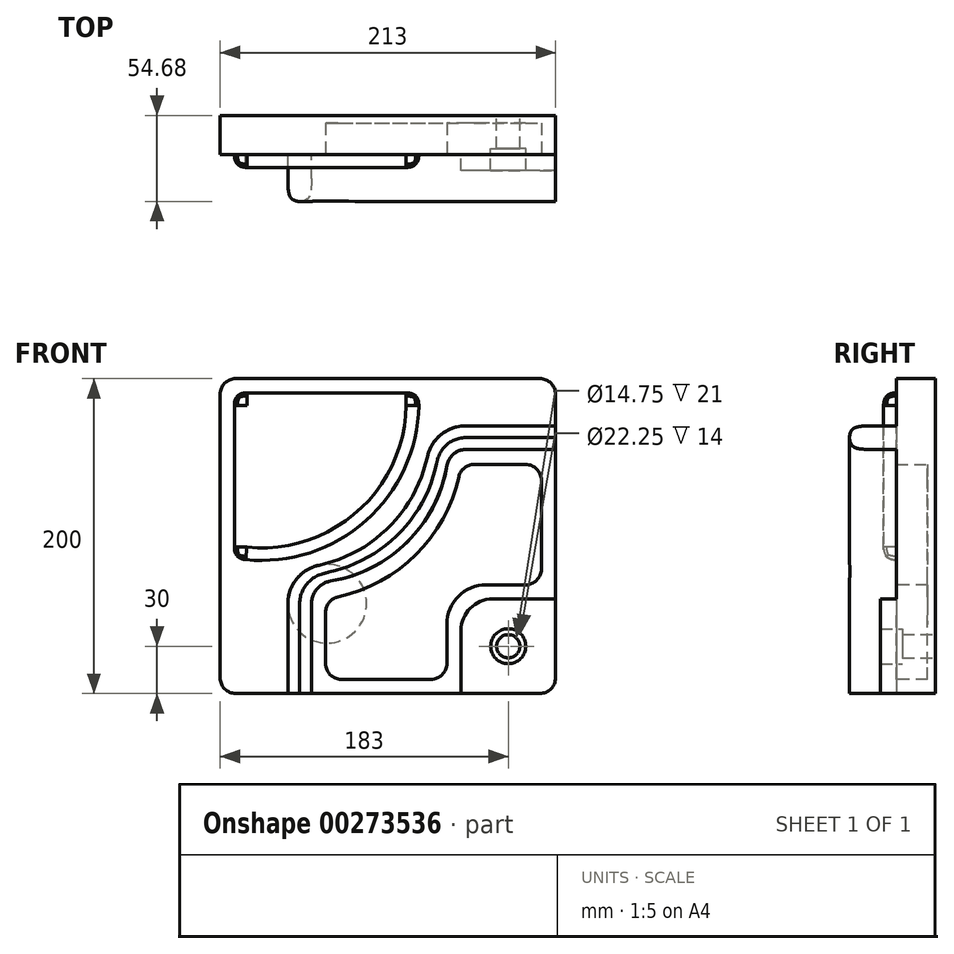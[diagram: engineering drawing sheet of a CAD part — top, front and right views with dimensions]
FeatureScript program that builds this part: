
annotation { "Feature Type Name" : "Feature", "Feature Type Description" : "" }
export const myFeature = defineFeature(function(context is Context, id is Id, definition is map)
    precondition{}
    {
        {
            var Q0;
            Q0=qCreatedBy(makeId("Front.planeOp"),FACE);
            var sketch = newSketch(context, id + "F0", { "sketchPlane" : qUnion([Q0])});
            skLineSegment(sketch, "E0", {"start": v(213, 0) * mm, "end": v(213, -200) * mm});
            skLineSegment(sketch, "E1", {"start": v(213, -200) * mm, "end": v(0, -200) * mm});
            skLineSegment(sketch, "E2", {"start": v(213, 0) * mm, "end": v(0, 0) * mm});
            skLineSegment(sketch, "E3", {"start": v(0, 0) * mm, "end": v(0, -200) * mm});
            skSolve(sketch);
        }
        {
            var Q0;
            Q0 = qSketchRegion(id + "F0", true);
            extrude(context, id + "F1", {"entities" : qUnion([Q0]), "oppositeDirection" : true, "depth" : 25 * mm});
        }
        {
            var Q0;
            Q0=makeQuery(id+"F1.opExtrude","CAP_FACE",FACE,{"disambiguationData":[OSD([sQuery(id+"F0.wireOp",EDGE,"E0"),sQuery(id+"F0.wireOp",EDGE,"E1"),sQuery(id+"F0.wireOp",EDGE,"E2"),sQuery(id+"F0.wireOp",EDGE,"E3")])],"isStart":true});
            var sketch = newSketch(context, id + "F2", { "sketchPlane" : qUnion([Q0])});
            skLineSegment(sketch, "E4", {"start": v(213, -200) * mm, "end": v(213, -140) * mm});
            skLineSegment(sketch, "E5", {"start": v(213, -140) * mm, "end": v(153, -140) * mm});
            skLineSegment(sketch, "E6", {"start": v(153, -140) * mm, "end": v(153, -200) * mm});
            skLineSegment(sketch, "E7", {"start": v(153, -200) * mm, "end": v(213, -200) * mm});
            skSolve(sketch);
        }
        {
            var Q0;
            Q0 = qSketchRegion(id + "F2", true);
            extrude(context, id + "F3", {"entities" : qUnion([Q0]), "operationType" : NewBodyOperationType.ADD, "depth" : 10 * mm});
        }
        {
            var Q0;
            Q0=makeQuery(id+"F3.boolean.opBoolean","MERGE",EDGE,{"derivedFrom":[makeQuery(id+"F1.opExtrude","SWEPT_EDGE",EDGE,{"disambiguationData":[OSD([sQuery(id+"F0.wireOp",EDGE,"E0"),sQuery(id+"F0.wireOp",EDGE,"E1")])]}),makeQuery(id+"F3.opExtrude","SWEPT_EDGE",EDGE,{"disambiguationData":[OSD([sQuery(id+"F2.wireOp",EDGE,"E4"),sQuery(id+"F2.wireOp",EDGE,"E7")])]})]});
            var Q1;
            Q1=makeQuery(id+"F1.opExtrude","SWEPT_EDGE",EDGE,{"disambiguationData":[OSD([sQuery(id+"F0.wireOp",EDGE,"E0"),sQuery(id+"F0.wireOp",EDGE,"E2")])]});
            var Q2;
            Q2=makeQuery(id+"F1.opExtrude","SWEPT_EDGE",EDGE,{"disambiguationData":[OSD([sQuery(id+"F0.wireOp",EDGE,"E2"),sQuery(id+"F0.wireOp",EDGE,"E3")])]});
            var Q3;
            Q3=makeQuery(id+"F1.opExtrude","SWEPT_EDGE",EDGE,{"disambiguationData":[OSD([sQuery(id+"F0.wireOp",EDGE,"E1"),sQuery(id+"F0.wireOp",EDGE,"E3")])]});
            fillet(context, id + "F4", {"entities" : qUnion([Q0, Q1, Q2, Q3]), "radius" : 10 * mm, "tangentPropagation" : true, "allowEdgeOverflow" : false});
        }
        {
            var Q0;
            Q0=makeQuery(id+"F1.opExtrude","CAP_FACE",FACE,{"disambiguationData":[OSD([sQuery(id+"F0.wireOp",EDGE,"E0"),sQuery(id+"F0.wireOp",EDGE,"E1"),sQuery(id+"F0.wireOp",EDGE,"E2"),sQuery(id+"F0.wireOp",EDGE,"E3")])],"isStart":true});
            var sketch = newSketch(context, id + "F5", { "sketchPlane" : qUnion([Q0])});
            skLineSegment(sketch, "E8", {"start": v(43, -143) * mm, "end": v(43, -200) * mm});
            skLineSegment(sketch, "E9", {"start": v(213, -30) * mm, "end": v(156, -30) * mm});
            skLineSegment(sketch, "E10", {"start": v(213, -30) * mm, "end": v(213, -45) * mm});
            skLineSegment(sketch, "E11", {"start": v(43, -200) * mm, "end": v(58, -200) * mm});
            skLineSegment(sketch, "E12", {"start": v(213, -45) * mm, "end": v(156, -45) * mm});
            skLineSegment(sketch, "E13", {"start": v(58, -200) * mm, "end": v(58, -143) * mm});
            skArc(sketch, "E14", {"start": v(70.2, -128.6) * mm, "mid": v(118.95, -103.6) * mm, "end": v(144.17, -54.98) * mm});
            skArc(sketch, "E15", {"start": v(62.7, -118.57) * mm, "mid": v(107.25, -94.25) * mm, "end": v(131.57, -49.7) * mm});
            skArc(sketch, "E16", {"start": v(156, -30) * mm, "mid": v(140.3, -35.54) * mm, "end": v(131.57, -49.7) * mm});
            skArc(sketch, "E17", {"start": v(62.7, -118.57) * mm, "mid": v(48.54, -127.3) * mm, "end": v(43, -143) * mm});
            skArc(sketch, "E18", {"start": v(70.2, -128.6) * mm, "mid": v(61.46, -133.57) * mm, "end": v(58, -143) * mm});
            skArc(sketch, "E19", {"start": v(156, -45) * mm, "mid": v(148.26, -47.83) * mm, "end": v(144.17, -54.98) * mm});
            skSolve(sketch);
        }
        {
            var Q0;
            Q0 = qSketchRegion(id + "F5", true);
            extrude(context, id + "F6", {"entities" : qUnion([Q0]), "operationType" : NewBodyOperationType.ADD, "depth" : 30 * mm});
        }
        {
            var Q0;
            Q0=makeQuery(id+"F6.opExtrude","CAP_EDGE",EDGE,{"disambiguationData":[OSD([sQuery(id+"F5.wireOp",EDGE,"E13")])],"isStart":false});
            var Q1;
            Q1=makeQuery(id+"F6.opExtrude","CAP_EDGE",EDGE,{"disambiguationData":[OSD([sQuery(id+"F5.wireOp",EDGE,"E8")])],"isStart":false});
            fillet(context, id + "F7", {"entities" : qUnion([Q0, Q1]), "radius" : 15 * mm, "tangentPropagation" : true, "rho" : 0.7, "crossSection" : FilletCrossSection.CONIC, "allowEdgeOverflow" : false});
        }
        {
            var Q0;
            Q0=makeQuery(id+"F3.opExtrude","CAP_FACE",FACE,{"disambiguationData":[OSD([sQuery(id+"F2.wireOp",EDGE,"E4"),sQuery(id+"F2.wireOp",EDGE,"E5"),sQuery(id+"F2.wireOp",EDGE,"E6"),sQuery(id+"F2.wireOp",EDGE,"E7")])],"isStart":false});
            var sketch = newSketch(context, id + "F8", { "sketchPlane" : qUnion([Q0])});
            skPoint(sketch, "E20", {"position": v(183, -170) * mm});
            skSolve(sketch);
        }
        {
            var Q0;
            Q0=sQuery(id+"F8.wireOp",VERTEX,"E20");
            var Q1;
            Q1=makeQuery(id+"F1.opExtrude","SWEPT_BODY",BODY,{"disambiguationData":[OSD([sQuery(id+"F0.wireOp",EDGE,"E0"),sQuery(id+"F0.wireOp",EDGE,"E1"),sQuery(id+"F0.wireOp",EDGE,"E2"),sQuery(id+"F0.wireOp",EDGE,"E3")])]});
            hole(context, id + "F9", {"style" : HoleStyle.C_BORE, "endStyle" : HoleEndStyle.THROUGH, "standardTappedOrClearance" : lookupTablePath({ "standard" : "ISO", "fit" : "Close", "size" : "M14", "type" : "Clearance" }), "standardBlindInLast" : lookupTablePath({ "fit" : "Close", "standard" : "ISO", "size" : "M14", "type" : "Clearance" }), "holeDiameter" : 14.75 * mm, "cBoreDiameter" : 22.25 * mm, "cBoreDepth" : 14 * mm, "tappedDepth" : 12 * mm, "tapClearance" : 3, "locations" : qUnion([Q0]), "scope" : qUnion([Q1])});
        }
        {
            var Q0;
            {var subQ0=sQuery(id+"F0.wireOp",EDGE,"E3");var subQ1=sQuery(id+"F0.wireOp",EDGE,"E2");var subQ2=sQuery(id+"F0.wireOp",EDGE,"E1");var subQ3=sQuery(id+"F0.wireOp",EDGE,"E0");Q0=makeQuery(id+"F6.boolean.opBoolean","SPLIT",FACE,{"disambiguationData":[TD([makeQuery(id+"F1.opExtrude","SWEPT_FACE",FACE,{"disambiguationData":[OSD([subQ1])]})])],"derivedFrom":makeQuery(id+"F1.opExtrude","CAP_FACE",FACE,{"disambiguationData":[OSD([subQ3,subQ2,subQ1,subQ0])],"isStart":true})});}
            var sketch = newSketch(context, id + "F10", { "sketchPlane" : qUnion([Q0])});
            skArc(sketch, "E21", {"start": v(67, -140) * mm, "mid": v(124.44, -111.77) * mm, "end": v(153, -54.5) * mm});
            skLineSegment(sketch, "E22", {"start": v(204, -54.5) * mm, "end": v(204, -131) * mm});
            skLineSegment(sketch, "E23", {"start": v(153, -54.5) * mm, "end": v(204, -54.5) * mm});
            skLineSegment(sketch, "E24", {"start": v(67, -191) * mm, "end": v(67, -140) * mm});
            skLineSegment(sketch, "E25", {"start": v(67, -191) * mm, "end": v(144, -191) * mm});
            skLineSegment(sketch, "E26", {"start": v(144, -191) * mm, "end": v(144, -131) * mm});
            skLineSegment(sketch, "E27", {"start": v(204, -131) * mm, "end": v(144, -131) * mm});
            skSolve(sketch);
        }
        {
            var Q0;
            Q0 = qSketchRegion(id + "F10", true);
            extrude(context, id + "F11", {"entities" : qUnion([Q0]), "operationType" : NewBodyOperationType.REMOVE, "oppositeDirection" : true, "depth" : 20 * mm});
        }
        {
            var Q0;
            Q0=makeQuery(id+"F11.boolean.opBoolean","COPY",EDGE,{"derivedFrom":makeQuery(id+"F11.opExtrude","SWEPT_EDGE",EDGE,{"disambiguationData":[OSD([sQuery(id+"F10.wireOp",EDGE,"E26"),sQuery(id+"F10.wireOp",EDGE,"E27")])]})});
            fillet(context, id + "F12", {"entities" : qUnion([Q0]), "radius" : 25 * mm, "tangentPropagation" : true, "allowEdgeOverflow" : false});
        }
        {
            var Q0;
            Q0=makeQuery(id+"F3.opExtrude","SWEPT_EDGE",EDGE,{"disambiguationData":[OSD([sQuery(id+"F2.wireOp",EDGE,"E5"),sQuery(id+"F2.wireOp",EDGE,"E6")])]});
            fillet(context, id + "F13", {"entities" : qUnion([Q0]), "radius" : 20 * mm, "tangentPropagation" : true, "allowEdgeOverflow" : false});
        }
        {
            var Q0;
            Q0=makeQuery(id+"F11.boolean.opBoolean","COPY",EDGE,{"derivedFrom":makeQuery(id+"F11.opExtrude","SWEPT_EDGE",EDGE,{"disambiguationData":[OSD([sQuery(id+"F10.wireOp",EDGE,"E22"),sQuery(id+"F10.wireOp",EDGE,"E23")])]})});
            var Q1;
            Q1=makeQuery(id+"F11.boolean.opBoolean","COPY",EDGE,{"derivedFrom":makeQuery(id+"F11.opExtrude","SWEPT_EDGE",EDGE,{"disambiguationData":[OSD([sQuery(id+"F10.wireOp",EDGE,"E21"),sQuery(id+"F10.wireOp",EDGE,"E23")])]})});
            var Q2;
            Q2=makeQuery(id+"F11.boolean.opBoolean","COPY",EDGE,{"derivedFrom":makeQuery(id+"F11.opExtrude","SWEPT_EDGE",EDGE,{"disambiguationData":[OSD([sQuery(id+"F10.wireOp",EDGE,"E21"),sQuery(id+"F10.wireOp",EDGE,"E24")])]})});
            var Q3;
            Q3=makeQuery(id+"F11.boolean.opBoolean","COPY",EDGE,{"derivedFrom":makeQuery(id+"F11.opExtrude","SWEPT_EDGE",EDGE,{"disambiguationData":[OSD([sQuery(id+"F10.wireOp",EDGE,"E24"),sQuery(id+"F10.wireOp",EDGE,"E25")])]})});
            var Q4;
            Q4=makeQuery(id+"F11.boolean.opBoolean","COPY",EDGE,{"derivedFrom":makeQuery(id+"F11.opExtrude","SWEPT_EDGE",EDGE,{"disambiguationData":[OSD([sQuery(id+"F10.wireOp",EDGE,"E22"),sQuery(id+"F10.wireOp",EDGE,"E27")])]})});
            var Q5;
            Q5=makeQuery(id+"F11.boolean.opBoolean","COPY",EDGE,{"derivedFrom":makeQuery(id+"F11.opExtrude","SWEPT_EDGE",EDGE,{"disambiguationData":[OSD([sQuery(id+"F10.wireOp",EDGE,"E25"),sQuery(id+"F10.wireOp",EDGE,"E26")])]})});
            fillet(context, id + "F14", {"entities" : qUnion([Q0, Q1, Q2, Q3, Q4, Q5]), "radius" : 10 * mm, "tangentPropagation" : true, "allowEdgeOverflow" : false});
        }
        {
            var Q0;
            {var subQ0=sQuery(id+"F0.wireOp",EDGE,"E3");var subQ1=sQuery(id+"F0.wireOp",EDGE,"E2");var subQ2=sQuery(id+"F0.wireOp",EDGE,"E1");var subQ3=sQuery(id+"F0.wireOp",EDGE,"E0");Q0=makeQuery(id+"F6.boolean.opBoolean","SPLIT",FACE,{"disambiguationData":[TD([makeQuery(id+"F1.opExtrude","SWEPT_FACE",FACE,{"disambiguationData":[OSD([subQ1])]})])],"derivedFrom":makeQuery(id+"F1.opExtrude","CAP_FACE",FACE,{"disambiguationData":[OSD([subQ3,subQ2,subQ1,subQ0])],"isStart":true})});}
            var sketch = newSketch(context, id + "F15", { "sketchPlane" : qUnion([Q0])});
            skLineSegment(sketch, "E28", {"start": v(9, -9) * mm, "end": v(126, -9) * mm});
            skLineSegment(sketch, "E29", {"start": v(9, -9) * mm, "end": v(9, -114) * mm});
            skArc(sketch, "E30", {"start": v(9, -114) * mm, "mid": v(93, -89.92) * mm, "end": v(126, -9) * mm});
            skSolve(sketch);
        }
        {
            var Q0;
            Q0 = qSketchRegion(id + "F15", true);
            extrude(context, id + "F16", {"entities" : qUnion([Q0]), "operationType" : NewBodyOperationType.ADD, "depth" : 8 * mm});
        }
        {
            var Q0;
            Q0=makeQuery(id+"F16.opExtrude","CAP_EDGE",EDGE,{"disambiguationData":[OSD([sQuery(id+"F15.wireOp",EDGE,"E30")])],"isStart":false});
            var Q1;
            Q1=makeQuery(id+"F16.opExtrude","SWEPT_EDGE",EDGE,{"disambiguationData":[OSD([sQuery(id+"F15.wireOp",EDGE,"E29"),sQuery(id+"F15.wireOp",EDGE,"E30")])]});
            var Q2;
            Q2=makeQuery(id+"F16.opExtrude","CAP_EDGE",EDGE,{"disambiguationData":[OSD([sQuery(id+"F15.wireOp",EDGE,"E29")])],"isStart":false});
            var Q3;
            Q3=makeQuery(id+"F16.opExtrude","SWEPT_EDGE",EDGE,{"disambiguationData":[OSD([sQuery(id+"F15.wireOp",EDGE,"E28"),sQuery(id+"F15.wireOp",EDGE,"E30")])]});
            var Q4;
            Q4=makeQuery(id+"F16.opExtrude","CAP_EDGE",EDGE,{"disambiguationData":[OSD([sQuery(id+"F15.wireOp",EDGE,"E28")])],"isStart":false});
            var Q5;
            Q5=makeQuery(id+"F16.opExtrude","SWEPT_EDGE",EDGE,{"disambiguationData":[OSD([sQuery(id+"F15.wireOp",EDGE,"E28"),sQuery(id+"F15.wireOp",EDGE,"E29")])]});
            fillet(context, id + "F17", {"entities" : qUnion([Q0, Q1, Q2, Q3, Q4, Q5]), "radius" : 8 * mm, "tangentPropagation" : true, "rho" : 0.5, "crossSection" : FilletCrossSection.CONIC, "allowEdgeOverflow" : false});
        }
    });
